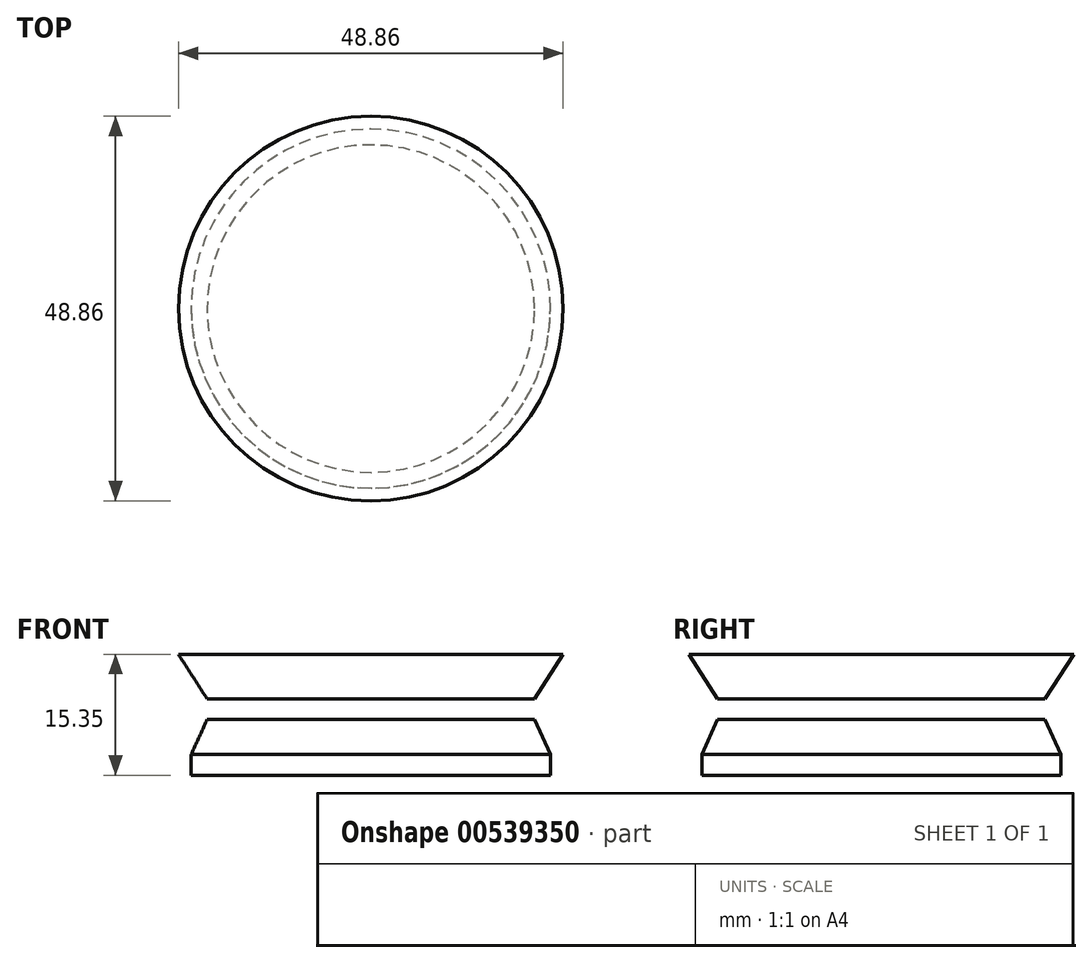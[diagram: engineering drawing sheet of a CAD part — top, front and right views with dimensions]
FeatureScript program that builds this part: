
annotation { "Feature Type Name" : "Feature", "Feature Type Description" : "" }
export const myFeature = defineFeature(function(context is Context, id is Id, definition is map)
    precondition{}
    {
        {
            var Q0;
            Q0=qCreatedBy(makeId("Right.planeOp"),FACE);
            var sketch = newSketch(context, id + "F0", { "sketchPlane" : qUnion([Q0])});
            skLineSegment(sketch, "E0", {"start": v(0, 31.1) * mm, "end": v(24.43, 31.1) * mm});
            skLineSegment(sketch, "E1", {"start": v(24.43, 31.1) * mm, "end": v(20.8, 25.44) * mm});
            skLineSegment(sketch, "E2", {"start": v(20.8, 25.44) * mm, "end": v(0, 25.44) * mm});
            skLineSegment(sketch, "E3", {"start": v(0, 25.44) * mm, "end": v(0, 31.1) * mm});
            skLineSegment(sketch, "E4", {"start": v(0, 22.82) * mm, "end": v(20.8, 22.82) * mm});
            skLineSegment(sketch, "E5", {"start": v(20.8, 22.82) * mm, "end": v(22.82, 18.37) * mm});
            skLineSegment(sketch, "E6", {"start": v(0, 15.75) * mm, "end": v(0, 22.82) * mm});
            skLineSegment(sketch, "E7", {"start": v(22.82, 18.37) * mm, "end": v(22.82, 15.75) * mm});
            skLineSegment(sketch, "E8", {"start": v(22.82, 15.75) * mm, "end": v(0, 15.75) * mm});
            skSolve(sketch);
        }
        {
            var Q0;
            Q0=makeQuery(id+"F0.imprint","IMPRINT",FACE,{"disambiguationData":[TD([[makeQuery(id+"F0.imprint","IMPRINT",EDGE,{"derivedFrom":sQuery(id+"F0.wireOp",EDGE,"E0")}),-1.0]])]});
            var Q1;
            Q1=makeQuery(id+"F0.imprint","IMPRINT",FACE,{"disambiguationData":[TD([[makeQuery(id+"F0.imprint","IMPRINT",EDGE,{"derivedFrom":sQuery(id+"F0.wireOp",EDGE,"E4")}),-1.0]])]});
            var Q2;
            Q2=sQuery(id+"F0.wireOp",EDGE,"E6");
            revolve(context, id + "F1", {"entities" : qUnion([Q0, Q1]), "axis" : qUnion([Q2]), "revolveType" : RevolveType.FULL});
        }
    });
